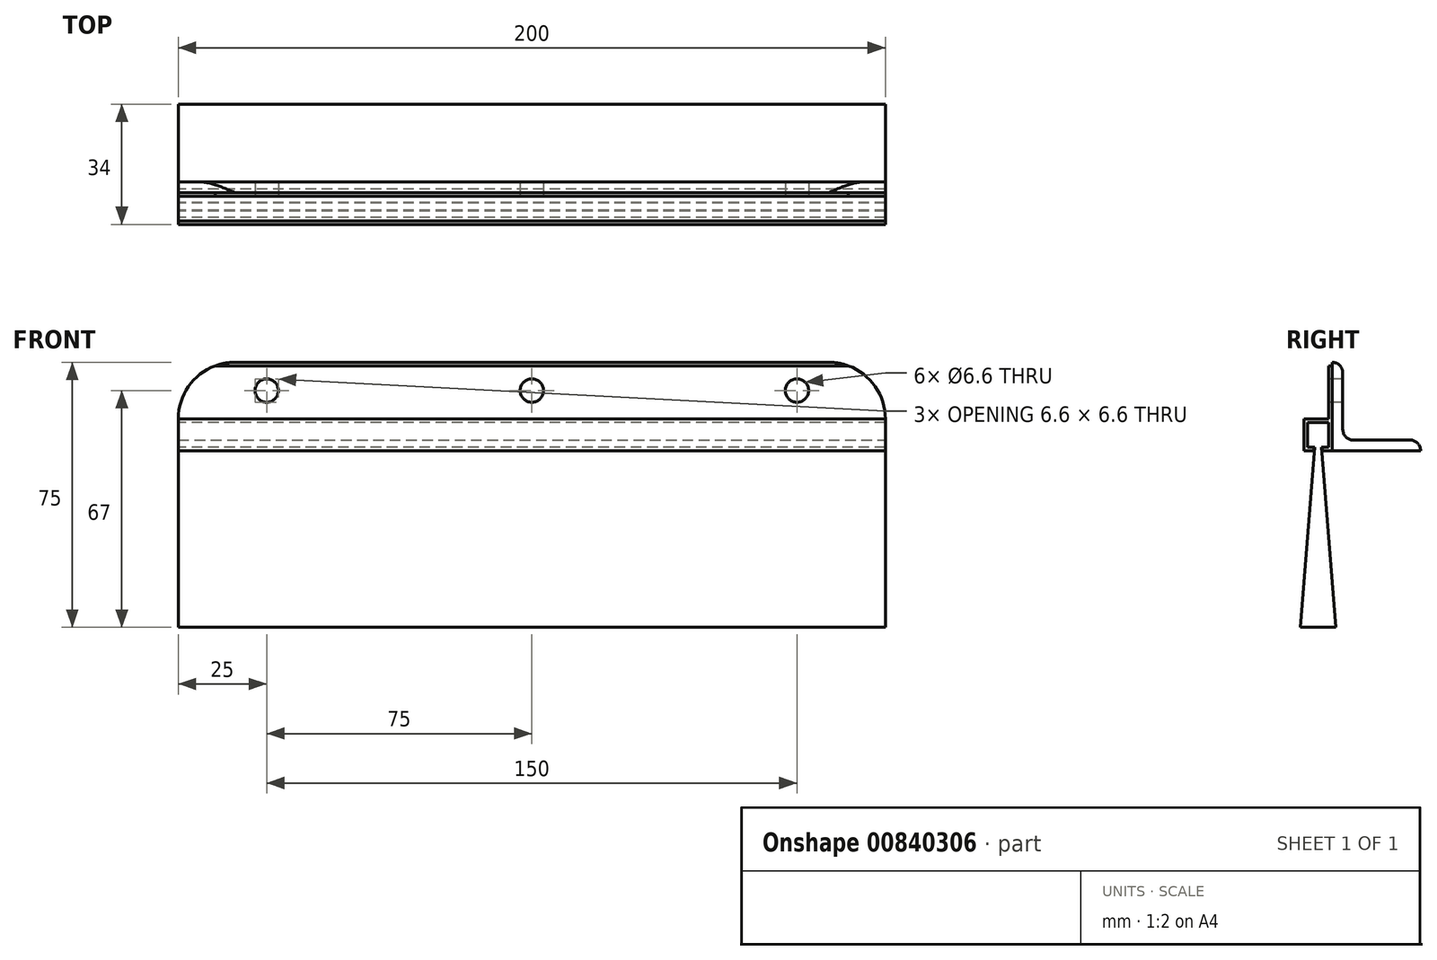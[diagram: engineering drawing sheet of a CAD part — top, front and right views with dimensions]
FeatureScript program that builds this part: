
annotation { "Feature Type Name" : "Feature", "Feature Type Description" : "" }
export const myFeature = defineFeature(function(context is Context, id is Id, definition is map)
    precondition{}
    {
        {
            var Q0;
            Q0=qCreatedBy(makeId("Right.planeOp"),FACE);
            var sketch = newSketch(context, id + "F0", { "sketchPlane" : qUnion([Q0])});
            skLineSegment(sketch, "E0", {"start": v(4, 24) * mm, "end": v(4, 0) * mm});
            skLineSegment(sketch, "E1", {"start": v(4, 0) * mm, "end": v(1.25, 0) * mm});
            skLineSegment(sketch, "E2", {"start": v(1.25, 0) * mm, "end": v(1.25, 1) * mm});
            skLineSegment(sketch, "E3", {"start": v(1.25, 1) * mm, "end": v(3, 1) * mm});
            skLineSegment(sketch, "E4", {"start": v(3, 1) * mm, "end": v(3, 8) * mm});
            skLineSegment(sketch, "E5", {"start": v(3, 8) * mm, "end": v(-3, 8) * mm});
            skLineSegment(sketch, "E6", {"start": v(-3, 8) * mm, "end": v(-3, 1) * mm});
            skLineSegment(sketch, "E7", {"start": v(-3, 1) * mm, "end": v(-1.25, 1) * mm});
            skLineSegment(sketch, "E8", {"start": v(-1.25, 1) * mm, "end": v(-1.25, 0) * mm});
            skLineSegment(sketch, "E9", {"start": v(-1.25, 0) * mm, "end": v(-4, 0) * mm});
            skLineSegment(sketch, "E10", {"start": v(-4, 0) * mm, "end": v(-4, 9) * mm});
            skLineSegment(sketch, "E11", {"start": v(-4, 9) * mm, "end": v(3, 9) * mm});
            skLineSegment(sketch, "E12", {"start": v(3, 9) * mm, "end": v(3, 24) * mm});
            skLineSegment(sketch, "E13", {"start": v(3, 24) * mm, "end": v(4, 24) * mm});
            skLineSegment(sketch, "E14", {"start": v(-3, 8) * mm, "end": v(-3, 9) * mm, "construction": true});
            skLineSegment(sketch, "E15", {"start": v(-3, 8) * mm, "end": v(-4, 8) * mm, "construction": true});
            skLineSegment(sketch, "E16", {"start": v(-1.25, 0) * mm, "end": v(1.25, 0) * mm, "construction": true});
            skSolve(sketch);
        }
        {
            var Q0;
            Q0 = qSketchRegion(id + "F0", true);
            extrude(context, id + "F1", {"entities" : qUnion([Q0]), "endBound" : BoundingType.SYMMETRIC, "depth" : 200 * mm, "offsetDistance" : 25 * mm});
        }
        {
            var Q0;
            Q0=qCreatedBy(makeId("Right.planeOp"),FACE);
            var sketch = newSketch(context, id + "F2", { "sketchPlane" : qUnion([Q0])});
            skLineSegment(sketch, "E17.bottom", {"start": v(-3, 8) * mm, "end": v(3, 8) * mm});
            skLineSegment(sketch, "E17.top", {"start": v(-3, 1) * mm, "end": v(-1, 1) * mm});
            skLineSegment(sketch, "E17.left", {"start": v(-3, 8) * mm, "end": v(-3, 1) * mm});
            skLineSegment(sketch, "E17.right", {"start": v(3, 8) * mm, "end": v(3, 1) * mm});
            skLineSegment(sketch, "E18", {"start": v(-1, 1) * mm, "end": v(-5, -50) * mm});
            skLineSegment(sketch, "E19", {"start": v(-5, -50) * mm, "end": v(5, -50) * mm});
            skLineSegment(sketch, "E20", {"start": v(5, -50) * mm, "end": v(1, 1) * mm});
            skLineSegment(sketch, "E21", {"start": v(0, -50) * mm, "end": v(0, 1) * mm, "construction": true});
            skLineSegment(sketch, "E22.trimOffspring", {"start": v(1, 1) * mm, "end": v(3, 1) * mm});
            skSolve(sketch);
        }
        {
            var Q0;
            Q0=makeQuery(id+"F2.imprint","IMPRINT",FACE,{"disambiguationData":[TD([[makeQuery(id+"F2.imprint","IMPRINT",EDGE,{"derivedFrom":sQuery(id+"F2.wireOp",EDGE,"E17.bottom")}),-1.0]])]});
            extrude(context, id + "F3", {"entities" : qUnion([Q0]), "endBound" : BoundingType.SYMMETRIC, "depth" : 200 * mm, "offsetDistance" : 25 * mm});
        }
        {
            var Q0;
            Q0=makeQuery(id+"F1.opExtrude","CAP_FACE",FACE,{"disambiguationData":[OSD([sQuery(id+"F0.wireOp",EDGE,"E0"),sQuery(id+"F0.wireOp",EDGE,"E1"),sQuery(id+"F0.wireOp",EDGE,"E2"),sQuery(id+"F0.wireOp",EDGE,"E3"),sQuery(id+"F0.wireOp",EDGE,"E4"),sQuery(id+"F0.wireOp",EDGE,"E5"),sQuery(id+"F0.wireOp",EDGE,"E6"),sQuery(id+"F0.wireOp",EDGE,"E7"),sQuery(id+"F0.wireOp",EDGE,"E8"),sQuery(id+"F0.wireOp",EDGE,"E9"),sQuery(id+"F0.wireOp",EDGE,"E10"),sQuery(id+"F0.wireOp",EDGE,"E11"),sQuery(id+"F0.wireOp",EDGE,"E12"),sQuery(id+"F0.wireOp",EDGE,"E13")])],"isStart":false});
            var sketch = newSketch(context, id + "F4", { "sketchPlane" : qUnion([Q0])});
            skLineSegment(sketch, "E23", {"start": v(4, 25) * mm, "end": v(4, 0) * mm});
            skLineSegment(sketch, "E24", {"start": v(4, 0) * mm, "end": v(29, 0) * mm});
            skLineSegment(sketch, "E25", {"start": v(29, 0) * mm, "end": v(29, 0) * mm});
            skLineSegment(sketch, "E26", {"start": v(26, 3) * mm, "end": v(10, 3) * mm});
            skLineSegment(sketch, "E27", {"start": v(7, 6) * mm, "end": v(7, 22) * mm});
            skLineSegment(sketch, "E28", {"start": v(4, 25) * mm, "end": v(4, 25) * mm});
            skPoint(sketch, "E29.visualSharp", {"position": v(7, 3) * mm});
            skArc(sketch, "E29.filletArc", {"start": v(7, 6) * mm, "mid": v(7.88, 3.88) * mm, "end": v(10, 3) * mm});
            skPoint(sketch, "E30.visualSharp", {"position": v(7, 25) * mm});
            skArc(sketch, "E30.filletArc", {"start": v(7, 22) * mm, "mid": v(6.12, 24.12) * mm, "end": v(4, 25) * mm});
            skPoint(sketch, "E31.visualSharp", {"position": v(29, 3) * mm});
            skArc(sketch, "E31.filletArc", {"start": v(29, 0) * mm, "mid": v(28.12, 2.12) * mm, "end": v(26, 3) * mm});
            skSolve(sketch);
        }
        {
            var Q0;
            Q0 = qSketchRegion(id + "F4", true);
            var Q1;
            Q1=makeQuery(id+"F1.opExtrude","CAP_FACE",FACE,{"disambiguationData":[OSD([sQuery(id+"F0.wireOp",EDGE,"E0"),sQuery(id+"F0.wireOp",EDGE,"E1"),sQuery(id+"F0.wireOp",EDGE,"E2"),sQuery(id+"F0.wireOp",EDGE,"E3"),sQuery(id+"F0.wireOp",EDGE,"E4"),sQuery(id+"F0.wireOp",EDGE,"E5"),sQuery(id+"F0.wireOp",EDGE,"E6"),sQuery(id+"F0.wireOp",EDGE,"E7"),sQuery(id+"F0.wireOp",EDGE,"E8"),sQuery(id+"F0.wireOp",EDGE,"E9"),sQuery(id+"F0.wireOp",EDGE,"E10"),sQuery(id+"F0.wireOp",EDGE,"E11"),sQuery(id+"F0.wireOp",EDGE,"E12"),sQuery(id+"F0.wireOp",EDGE,"E13")])],"isStart":true});
            extrude(context, id + "F5", {"entities" : qUnion([Q0]), "endBound" : BoundingType.UP_TO_SURFACE, "oppositeDirection" : true, "depth" : 25 * mm, "endBoundEntityFace" : qUnion([Q1]), "offsetDistance" : 25 * mm});
        }
        {
            var Q0;
            Q0=makeQuery(id+"F1.opExtrude","SWEPT_FACE",FACE,{"disambiguationData":[OSD([sQuery(id+"F0.wireOp",EDGE,"E12")])]});
            var sketch = newSketch(context, id + "F6", { "sketchPlane" : qUnion([Q0])});
            skPoint(sketch, "E32", {"position": v(-75, 17) * mm});
            skPoint(sketch, "E33", {"position": v(0, 17) * mm});
            skPoint(sketch, "E34", {"position": v(75, 17) * mm});
            skSolve(sketch);
        }
        {
            var Q0;
            Q0=sQuery(id+"F6.wireOp",VERTEX,"E32");
            var Q1;
            Q1=sQuery(id+"F6.wireOp",VERTEX,"E33");
            var Q2;
            Q2=sQuery(id+"F6.wireOp",VERTEX,"E34");
            var Q3;
            Q3=makeQuery(id+"F1.opExtrude","SWEPT_BODY",BODY,{"disambiguationData":[OSD([sQuery(id+"F0.wireOp",EDGE,"E0"),sQuery(id+"F0.wireOp",EDGE,"E1"),sQuery(id+"F0.wireOp",EDGE,"E2"),sQuery(id+"F0.wireOp",EDGE,"E3"),sQuery(id+"F0.wireOp",EDGE,"E4"),sQuery(id+"F0.wireOp",EDGE,"E5"),sQuery(id+"F0.wireOp",EDGE,"E6"),sQuery(id+"F0.wireOp",EDGE,"E7"),sQuery(id+"F0.wireOp",EDGE,"E8"),sQuery(id+"F0.wireOp",EDGE,"E9"),sQuery(id+"F0.wireOp",EDGE,"E10"),sQuery(id+"F0.wireOp",EDGE,"E11"),sQuery(id+"F0.wireOp",EDGE,"E12"),sQuery(id+"F0.wireOp",EDGE,"E13")])]});
            var Q4;
            Q4=makeQuery(id+"F5.opExtrude","SWEPT_BODY",BODY,{"disambiguationData":[OSD([sQuery(id+"F4.wireOp",EDGE,"E23"),sQuery(id+"F4.wireOp",EDGE,"E24"),sQuery(id+"F4.wireOp",EDGE,"E26"),sQuery(id+"F4.wireOp",EDGE,"E27"),sQuery(id+"F4.wireOp",EDGE,"E29.filletArc"),sQuery(id+"F4.wireOp",EDGE,"E30.filletArc"),sQuery(id+"F4.wireOp",EDGE,"E31.filletArc")])]});
            hole(context, id + "F7", {"style" : HoleStyle.SIMPLE, "endStyle" : HoleEndStyle.THROUGH, "standardTappedOrClearance" : lookupTablePath({ "fit" : "Normal", "standard" : "ISO", "size" : "M6", "type" : "Clearance" }), "standardBlindInLast" : lookupTablePath({ "fit" : "Normal", "standard" : "ISO", "size" : "M6", "type" : "Clearance" }), "holeDiameter" : 6.6 * mm, "majorDiameter" : 5 * mm, "isTappedThrough" : true, "tappedDepth" : 12 * mm, "tapClearance" : 3, "startFromSketch" : true, "locations" : qUnion([Q0, Q1, Q2]), "scope" : qUnion([Q3, Q4])});
        }
        {
            var Q0;
            Q0=makeQuery(id+"F1.opExtrude","SWEPT_FACE",FACE,{"disambiguationData":[OSD([sQuery(id+"F0.wireOp",EDGE,"E12")])]});
            var sketch = newSketch(context, id + "F8", { "sketchPlane" : qUnion([Q0])});
            skArc(sketch, "E35", {"start": v(-84, 25) * mm, "mid": v(-95.31, 20.31) * mm, "end": v(-100, 9) * mm});
            skLineSegment(sketch, "E36", {"start": v(-84, 25) * mm, "end": v(-100, 25) * mm});
            skLineSegment(sketch, "E37", {"start": v(-100, 25) * mm, "end": v(-100, 9) * mm});
            skArc(sketch, "E38.MirrorCS", {"start": v(84, 25) * mm, "mid": v(95.31, 20.31) * mm, "end": v(100, 9) * mm});
            skLineSegment(sketch, "E39.MirrorCS", {"start": v(84, 25) * mm, "end": v(100, 25) * mm});
            skLineSegment(sketch, "E40.MirrorCS", {"start": v(100, 25) * mm, "end": v(100, 9) * mm});
            skSolve(sketch);
        }
        {
            var Q0;
            Q0 = qSketchRegion(id + "F8", true);
            extrude(context, id + "F9", {"entities" : qUnion([Q0]), "operationType" : NewBodyOperationType.REMOVE, "endBound" : BoundingType.THROUGH_ALL, "oppositeDirection" : true, "depth" : 25 * mm, "offsetDistance" : 25 * mm});
        }
    });
